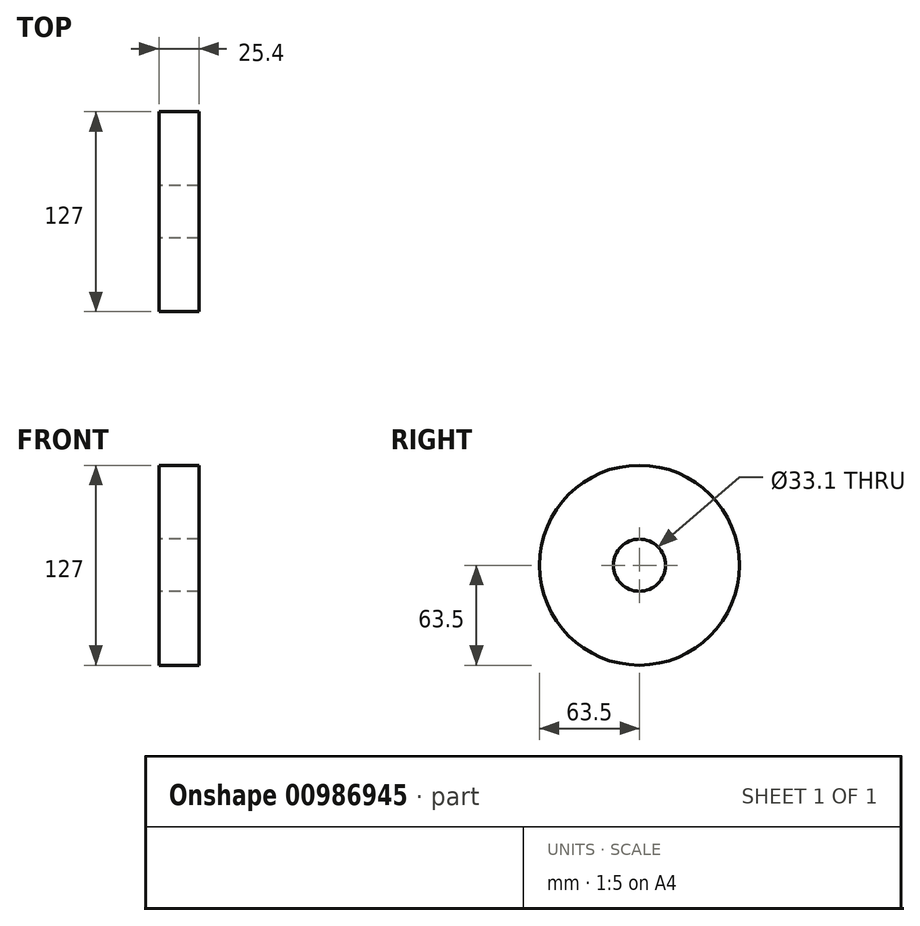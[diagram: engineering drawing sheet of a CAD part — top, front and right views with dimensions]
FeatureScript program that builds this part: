
annotation { "Feature Type Name" : "Feature", "Feature Type Description" : "" }
export const myFeature = defineFeature(function(context is Context, id is Id, definition is map)
    precondition{}
    {
        {
            var Q0;
            Q0=qCreatedBy(makeId("Right.planeOp"),FACE);
            var sketch = newSketch(context, id + "F0", { "sketchPlane" : qUnion([Q0])});
            skCircle(sketch, "E0", {"center": v(0, 0) * mm, "radius": 63.5 * mm});
            skSolve(sketch);
        }
        {
            var Q0;
            Q0 = qSketchRegion(id + "F0", true);
            extrude(context, id + "F1", {"entities" : qUnion([Q0]), "depth" : 25.4 * mm, "offsetDistance" : 25.4 * mm});
        }
        {
            var Q0;
            Q0=makeQuery(id+"F1.opExtrude","CAP_FACE",FACE,{"disambiguationData":[OSD([sQuery(id+"F0.wireOp",EDGE,"E0")])],"isStart":true});
            var sketch = newSketch(context, id + "F2", { "sketchPlane" : qUnion([Q0])});
            skCircle(sketch, "E1", {"center": v(0, 0) * mm, "radius": 16.55 * mm});
            skSolve(sketch);
        }
        {
            var Q0;
            Q0=makeQuery(id+"F2.imprint","IMPRINT",FACE,{"disambiguationData":[TD([[makeQuery(id+"F2.imprint","IMPRINT",EDGE,{"derivedFrom":sQuery(id+"F2.wireOp",EDGE,"E1")}),1.0]])]});
            extrude(context, id + "F3", {"entities" : qUnion([Q0]), "operationType" : NewBodyOperationType.REMOVE, "oppositeDirection" : true, "depth" : 25.4 * mm, "offsetDistance" : 25.4 * mm});
        }
    });
